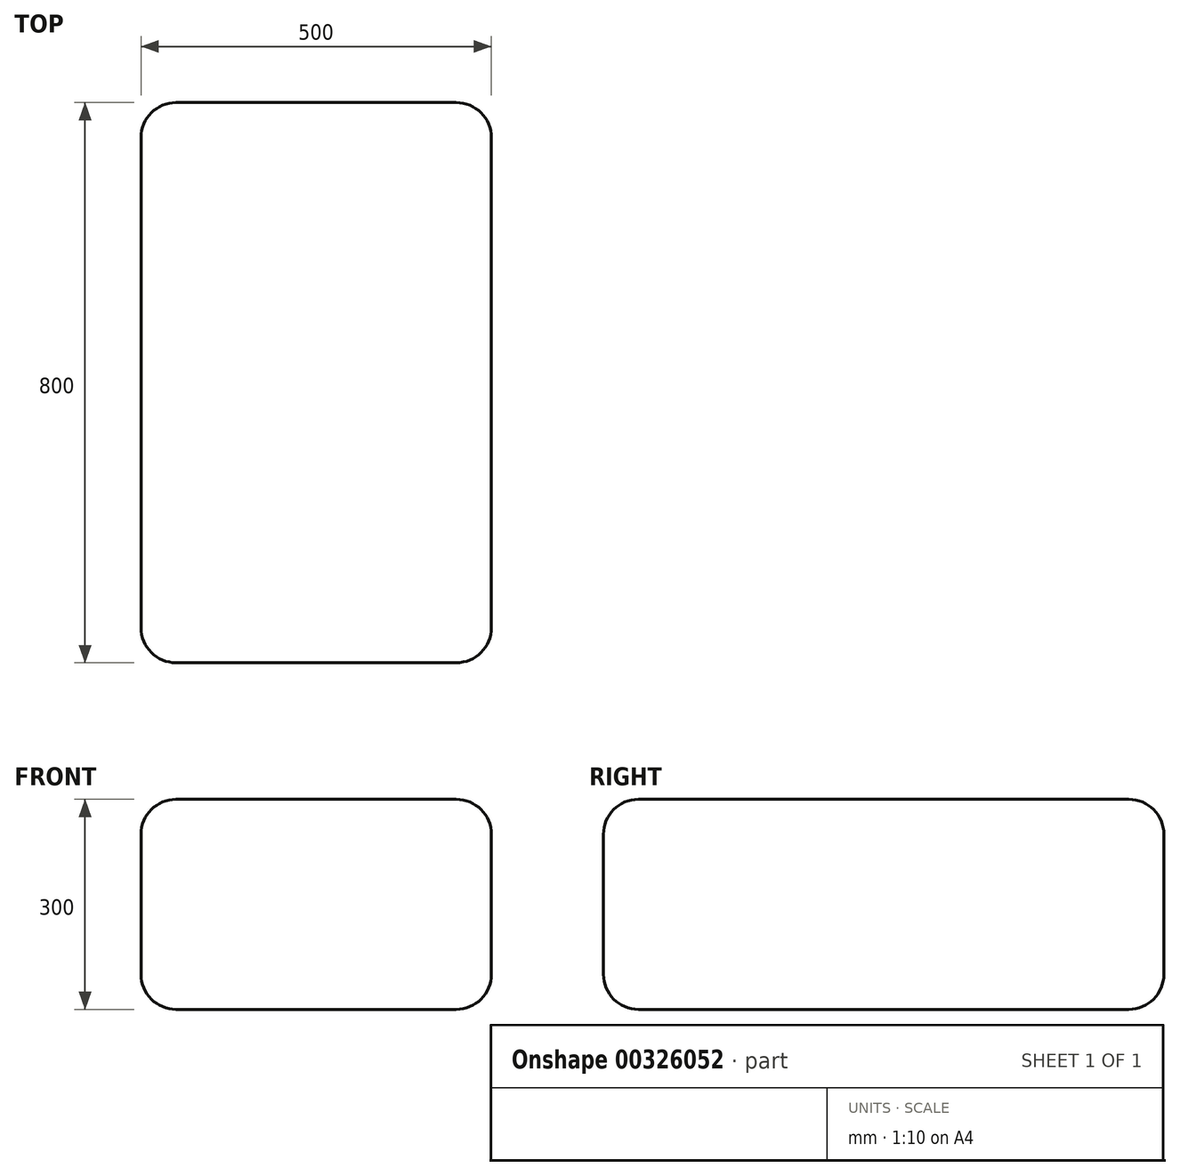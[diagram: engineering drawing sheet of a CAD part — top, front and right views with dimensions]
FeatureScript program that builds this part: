
annotation { "Feature Type Name" : "Feature", "Feature Type Description" : "" }
export const myFeature = defineFeature(function(context is Context, id is Id, definition is map)
    precondition{}
    {
        {
            var Q0;
            Q0=qCreatedBy(makeId("Top.planeOp"),FACE);
            var sketch = newSketch(context, id + "F0", { "sketchPlane" : qUnion([Q0])});
            skLineSegment(sketch, "E0.bottom", {"start": v(-250, 400) * mm, "end": v(250, 400) * mm});
            skLineSegment(sketch, "E0.top", {"start": v(-250, -400) * mm, "end": v(250, -400) * mm});
            skLineSegment(sketch, "E0.left", {"start": v(-250, 400) * mm, "end": v(-250, -400) * mm});
            skLineSegment(sketch, "E0.right", {"start": v(250, 400) * mm, "end": v(250, -400) * mm});
            skPoint(sketch, "E0.middle", {"position": v(0, 0) * mm});
            skSolve(sketch);
        }
        {
            var Q0;
            Q0 = qSketchRegion(id + "F0", true);
            extrude(context, id + "F1", {"entities" : qUnion([Q0]), "endBound" : BoundingType.SYMMETRIC, "depth" : 300 * mm});
        }
        {
            var Q0;
            Q0=makeQuery(id+"F1.opExtrude","SWEPT_FACE",FACE,{"disambiguationData":[OSD([sQuery(id+"F0.wireOp",EDGE,"E0.top")])]});
            var Q1;
            Q1=makeQuery(id+"F1.opExtrude","CAP_FACE",FACE,{"disambiguationData":[OSD([sQuery(id+"F0.wireOp",EDGE,"E0.bottom"),sQuery(id+"F0.wireOp",EDGE,"E0.top"),sQuery(id+"F0.wireOp",EDGE,"E0.left"),sQuery(id+"F0.wireOp",EDGE,"E0.right")])],"isStart":false});
            var Q2;
            Q2=makeQuery(id+"F1.opExtrude","SWEPT_FACE",FACE,{"disambiguationData":[OSD([sQuery(id+"F0.wireOp",EDGE,"E0.right")])]});
            var Q3;
            Q3=makeQuery(id+"F1.opExtrude","SWEPT_FACE",FACE,{"disambiguationData":[OSD([sQuery(id+"F0.wireOp",EDGE,"E0.left")])]});
            var Q4;
            Q4=makeQuery(id+"F1.opExtrude","CAP_EDGE",EDGE,{"disambiguationData":[OSD([sQuery(id+"F0.wireOp",EDGE,"E0.right")])],"isStart":true});
            var Q5;
            Q5=makeQuery(id+"F1.opExtrude","SWEPT_FACE",FACE,{"disambiguationData":[OSD([sQuery(id+"F0.wireOp",EDGE,"E0.bottom")])]});
            fillet(context, id + "F2", {"entities" : qUnion([Q0, Q1, Q2, Q3, Q4, Q5]), "radius" : 50 * mm, "tangentPropagation" : true, "allowEdgeOverflow" : false});
        }
    });
